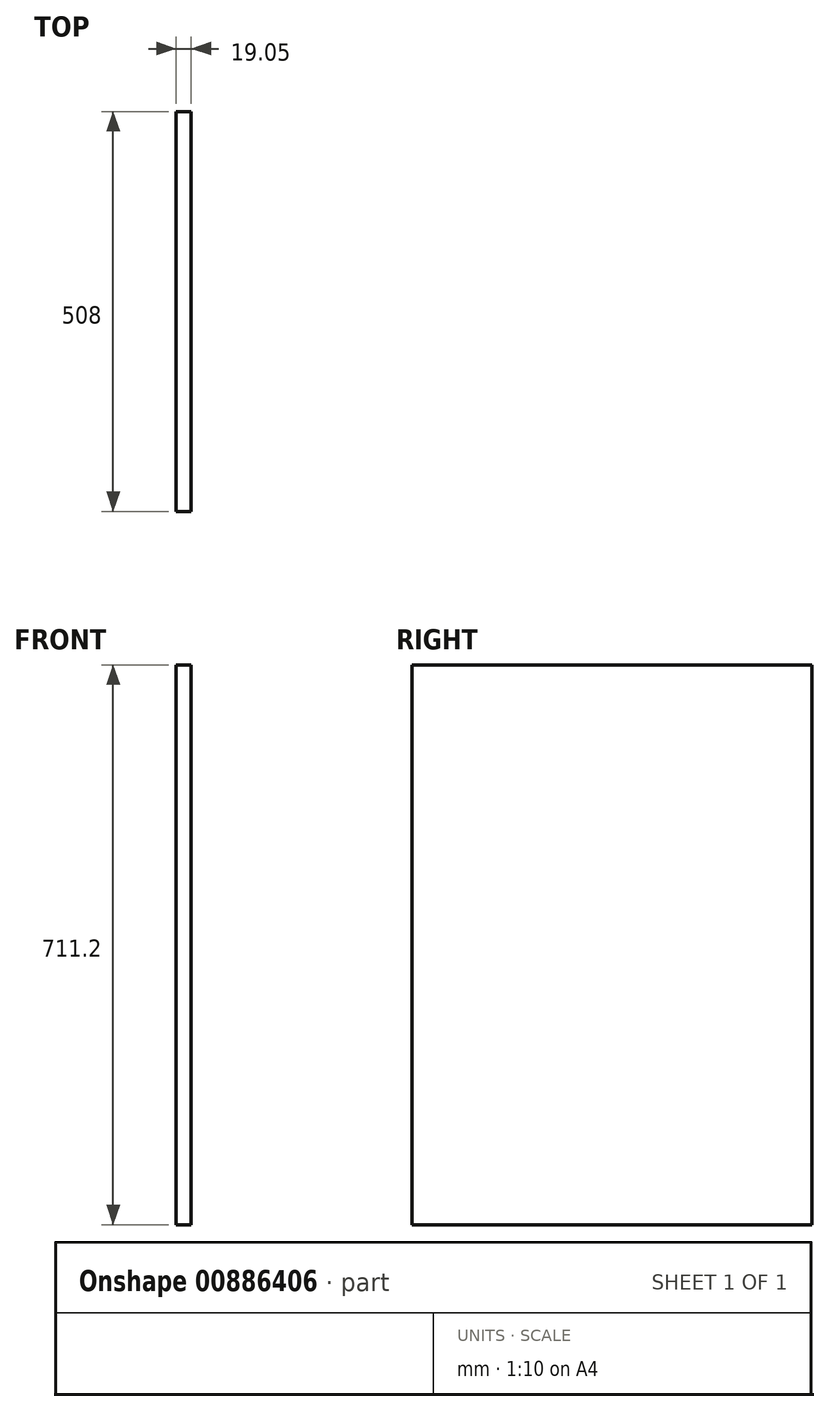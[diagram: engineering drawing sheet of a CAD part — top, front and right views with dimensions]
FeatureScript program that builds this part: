
annotation { "Feature Type Name" : "Feature", "Feature Type Description" : "" }
export const myFeature = defineFeature(function(context is Context, id is Id, definition is map)
    precondition{}
    {
        {
            var Q0;
            Q0=qCreatedBy(makeId("Right.planeOp"),FACE);
            var sketch = newSketch(context, id + "F0", { "sketchPlane" : qUnion([Q0])});
            skLineSegment(sketch, "E0.bottom", {"start": v(254, 355.6) * mm, "end": v(-254, 355.6) * mm});
            skLineSegment(sketch, "E0.top", {"start": v(254, -355.6) * mm, "end": v(-254, -355.6) * mm});
            skLineSegment(sketch, "E0.left", {"start": v(254, 355.6) * mm, "end": v(254, -355.6) * mm});
            skLineSegment(sketch, "E0.right", {"start": v(-254, 355.6) * mm, "end": v(-254, -355.6) * mm});
            skPoint(sketch, "E0.middle", {"position": v(0, 0) * mm});
            skSolve(sketch);
        }
        {
            var Q0;
            Q0=makeQuery(id+"F0.imprint","IMPRINT",FACE,{"disambiguationData":[TD([[makeQuery(id+"F0.imprint","IMPRINT",EDGE,{"derivedFrom":sQuery(id+"F0.wireOp",EDGE,"E0.top")}),-1.0]])]});
            extrude(context, id + "F1", {"entities" : qUnion([Q0]), "depth" : 19.05 * mm, "offsetDistance" : 25.4 * mm});
        }
    });
